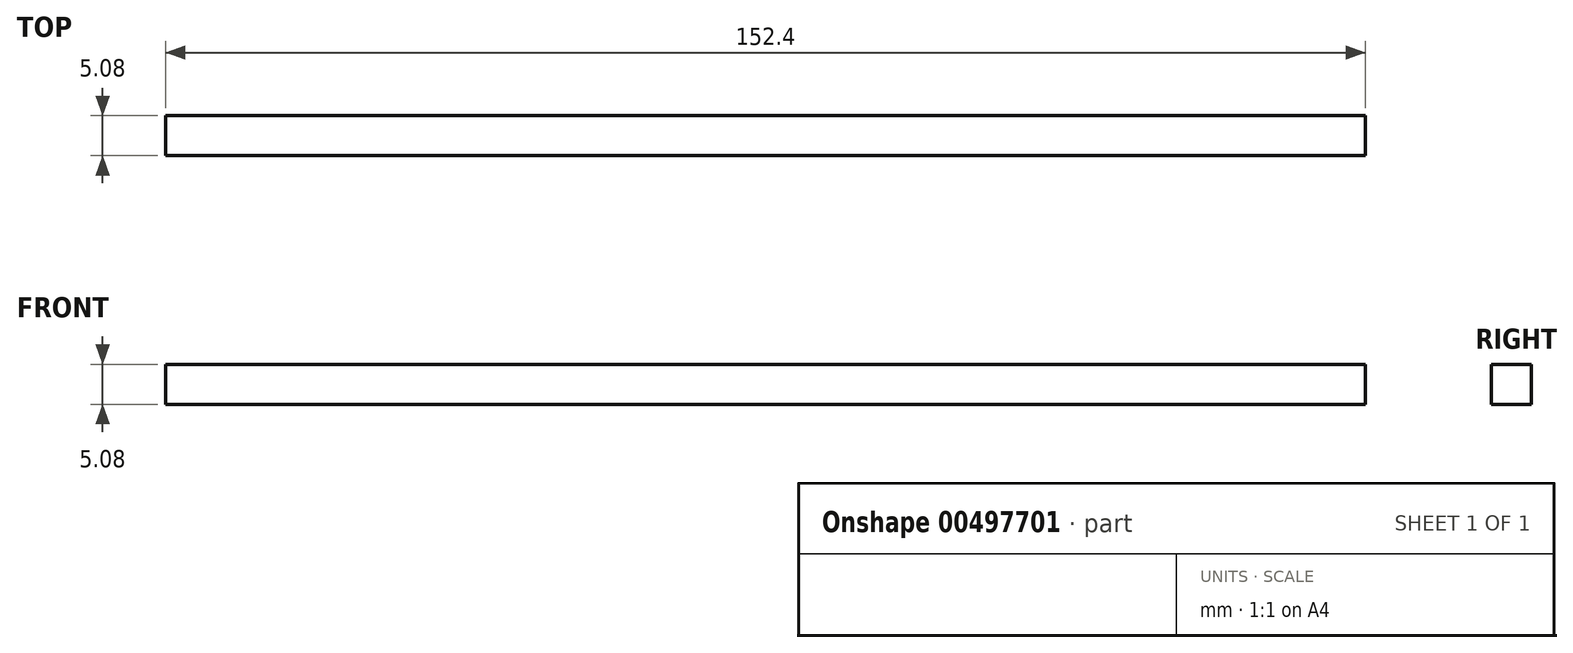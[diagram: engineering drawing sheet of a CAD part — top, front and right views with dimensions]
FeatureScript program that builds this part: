
annotation { "Feature Type Name" : "Feature", "Feature Type Description" : "" }
export const myFeature = defineFeature(function(context is Context, id is Id, definition is map)
    precondition{}
    {
        {
            var Q0;
            Q0=qCreatedBy(makeId("Top.planeOp"),FACE);
            var sketch = newSketch(context, id + "F0", { "sketchPlane" : qUnion([Q0])});
            skLineSegment(sketch, "E0.bottom", {"start": v(83, 22.79) * mm, "end": v(-69.4, 22.79) * mm});
            skLineSegment(sketch, "E0.top", {"start": v(83, 27.87) * mm, "end": v(-69.4, 27.87) * mm});
            skLineSegment(sketch, "E0.left", {"start": v(83, 22.79) * mm, "end": v(83, 27.87) * mm});
            skLineSegment(sketch, "E0.right", {"start": v(-69.4, 22.79) * mm, "end": v(-69.4, 27.87) * mm});
            skPoint(sketch, "E0.middle", {"position": v(6.8, 25.33) * mm});
            skSolve(sketch);
        }
        {
            var Q0;
            Q0 = qSketchRegion(id + "F0", true);
            extrude(context, id + "F1", {"entities" : qUnion([Q0]), "depth" : 5.08 * mm, "offsetDistance" : 25.4 * mm});
        }
    });
